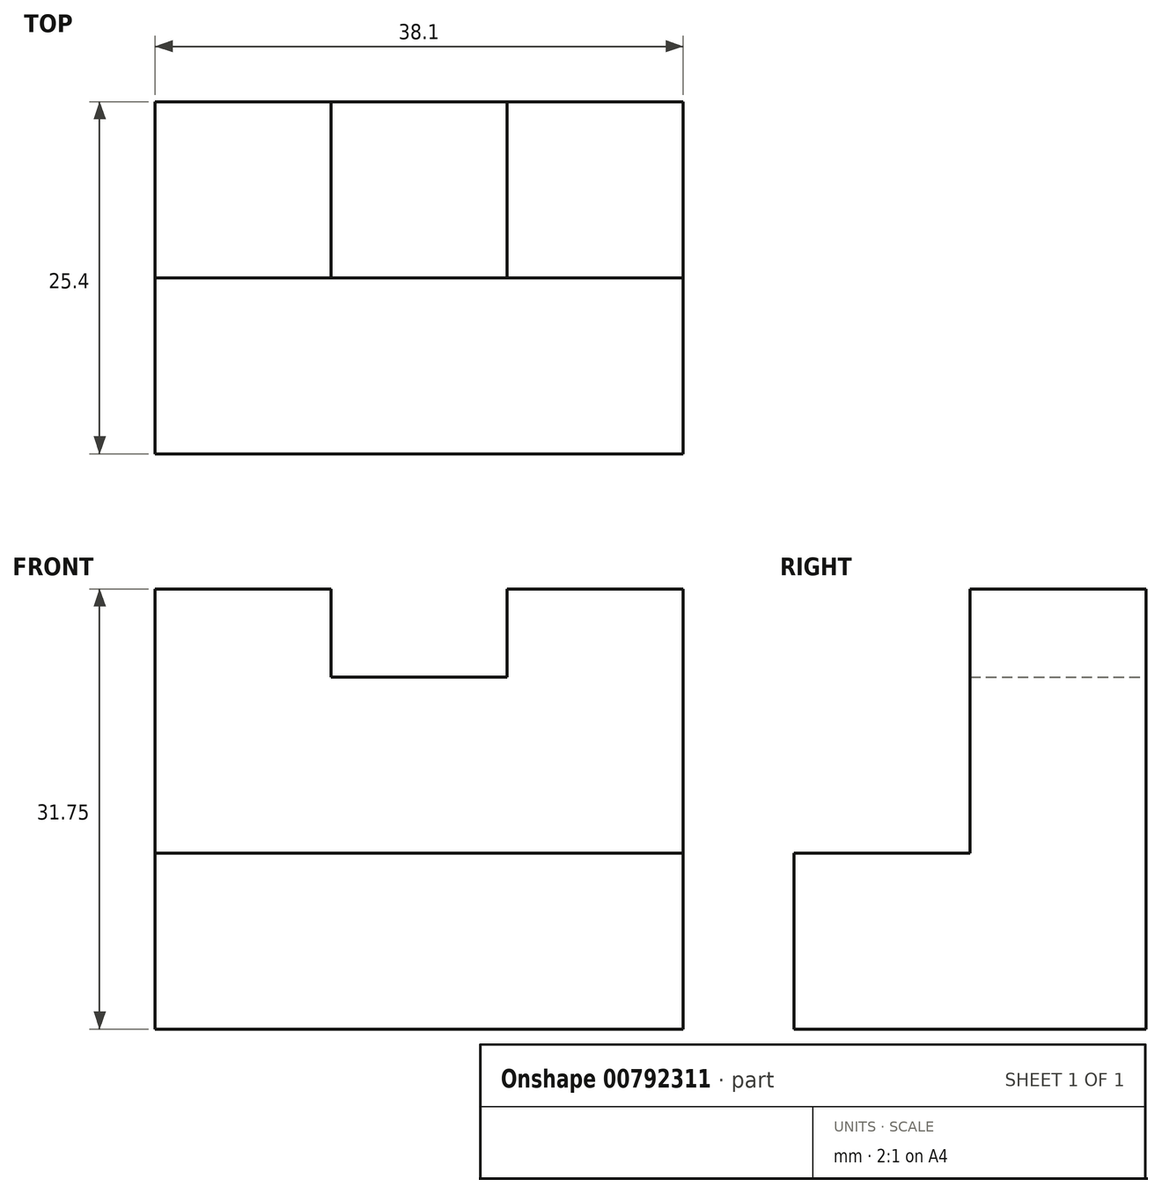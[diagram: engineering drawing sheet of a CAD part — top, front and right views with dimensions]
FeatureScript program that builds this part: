
annotation { "Feature Type Name" : "Feature", "Feature Type Description" : "" }
export const myFeature = defineFeature(function(context is Context, id is Id, definition is map)
    precondition{}
    {
        {
            var Q0;
            Q0=qCreatedBy(makeId("Top.planeOp"),FACE);
            var sketch = newSketch(context, id + "F0", { "sketchPlane" : qUnion([Q0])});
            skLineSegment(sketch, "E0.bottom", {"start": v(38.1, 36.92) * mm, "end": v(0, 36.92) * mm});
            skLineSegment(sketch, "E0.top", {"start": v(38.1, 11.52) * mm, "end": v(0, 11.52) * mm});
            skLineSegment(sketch, "E0.left", {"start": v(38.1, 36.92) * mm, "end": v(38.1, 11.52) * mm});
            skLineSegment(sketch, "E0.right", {"start": v(0, 36.92) * mm, "end": v(0, 11.52) * mm});
            skSolve(sketch);
        }
        {
            var Q0;
            Q0=qSketchRegion(id+"F0",true);
            extrude(context, id + "F1", {"entities" : qUnion([Q0]), "depth" : 31.75 * mm, "offsetDistance" : 25.4 * mm});
        }
        {
            var Q0;
            Q0=makeQuery(id+"F1.opExtrude","CAP_FACE",FACE,{"disambiguationData":[OSD([sQuery(id+"F0.wireOp",EDGE,"E0.bottom"),sQuery(id+"F0.wireOp",EDGE,"E0.top"),sQuery(id+"F0.wireOp",EDGE,"E0.left"),sQuery(id+"F0.wireOp",EDGE,"E0.right")])],"isStart":false});
            var sketch = newSketch(context, id + "F2", { "sketchPlane" : qUnion([Q0])});
            skLineSegment(sketch, "E1.bottom", {"start": v(38.1, 24.22) * mm, "end": v(0, 24.22) * mm});
            skLineSegment(sketch, "E1.top", {"start": v(38.1, 11.52) * mm, "end": v(0, 11.52) * mm});
            skLineSegment(sketch, "E1.left", {"start": v(38.1, 24.22) * mm, "end": v(38.1, 11.52) * mm});
            skLineSegment(sketch, "E1.right", {"start": v(0, 24.22) * mm, "end": v(0, 11.52) * mm});
            skSolve(sketch);
        }
        {
            var Q0;
            Q0=makeQuery(id+"F2.imprint","IMPRINT",FACE,{"disambiguationData":[TD([[makeQuery(id+"F2.imprint","IMPRINT",EDGE,{"derivedFrom":sQuery(id+"F2.wireOp",EDGE,"E1.bottom")}),1.0]])]});
            extrude(context, id + "F3", {"entities" : qUnion([Q0]), "operationType" : NewBodyOperationType.REMOVE, "oppositeDirection" : true, "depth" : 19.05 * mm, "offsetDistance" : 25.4 * mm});
        }
        {
            var Q0;
            Q0=makeQuery(id+"F1.opExtrude","CAP_FACE",FACE,{"disambiguationData":[OSD([sQuery(id+"F0.wireOp",EDGE,"E0.bottom"),sQuery(id+"F0.wireOp",EDGE,"E0.top"),sQuery(id+"F0.wireOp",EDGE,"E0.left"),sQuery(id+"F0.wireOp",EDGE,"E0.right")])],"isStart":false});
            var sketch = newSketch(context, id + "F4", { "sketchPlane" : qUnion([Q0])});
            skLineSegment(sketch, "E2", {"start": v(0, 24.22) * mm, "end": v(12.7, 24.22) * mm});
            skLineSegment(sketch, "E3.bottom", {"start": v(12.7, 24.22) * mm, "end": v(25.4, 24.22) * mm});
            skLineSegment(sketch, "E3.top", {"start": v(12.7, 36.92) * mm, "end": v(25.4, 36.92) * mm});
            skLineSegment(sketch, "E3.left", {"start": v(12.7, 24.22) * mm, "end": v(12.7, 36.92) * mm});
            skLineSegment(sketch, "E3.right", {"start": v(25.4, 24.22) * mm, "end": v(25.4, 36.92) * mm});
            skSolve(sketch);
        }
        {
            var Q0;
            Q0=makeQuery(id+"F4.imprint","IMPRINT",FACE,{"disambiguationData":[TD([[makeQuery(id+"F4.imprint","IMPRINT",EDGE,{"derivedFrom":sQuery(id+"F4.wireOp",EDGE,"E3.bottom")}),-1.0]])]});
            extrude(context, id + "F5", {"entities" : qUnion([Q0]), "operationType" : NewBodyOperationType.REMOVE, "oppositeDirection" : true, "depth" : 6.35 * mm, "offsetDistance" : 25.4 * mm});
        }
    });
